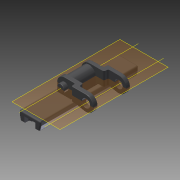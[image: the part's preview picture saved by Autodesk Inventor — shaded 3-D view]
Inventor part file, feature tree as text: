
AUTODESK INVENTOR PART (.ipt)
format: ipt  version: 2015 SP1 (Build 190203100, 203)  size: 570,368 bytes
history: native  units: in
note: dims shown in document units (in); Inventor stores cm internally (conversion verified against a paired STEP export)
features: other x4, plane x1, imported_body x1
ambient origin geometry x8: Origin, YZ Plane, XZ Plane, XY Plane, X Axis, Y Axis, Z Axis, Center Point
bodies: Body1 (feature_tree)
feature tree (6):
  other  "Chain Paddle Base"
  parser-record x1  (decoder bookkeeping rows leaked as tree rows — omitted from the tree; the rows remain in map.json)
  plane  "Work Plane1"
  imported_body  "Base1"
  other  "Work Axis1"
  other  "Work Axis2"
